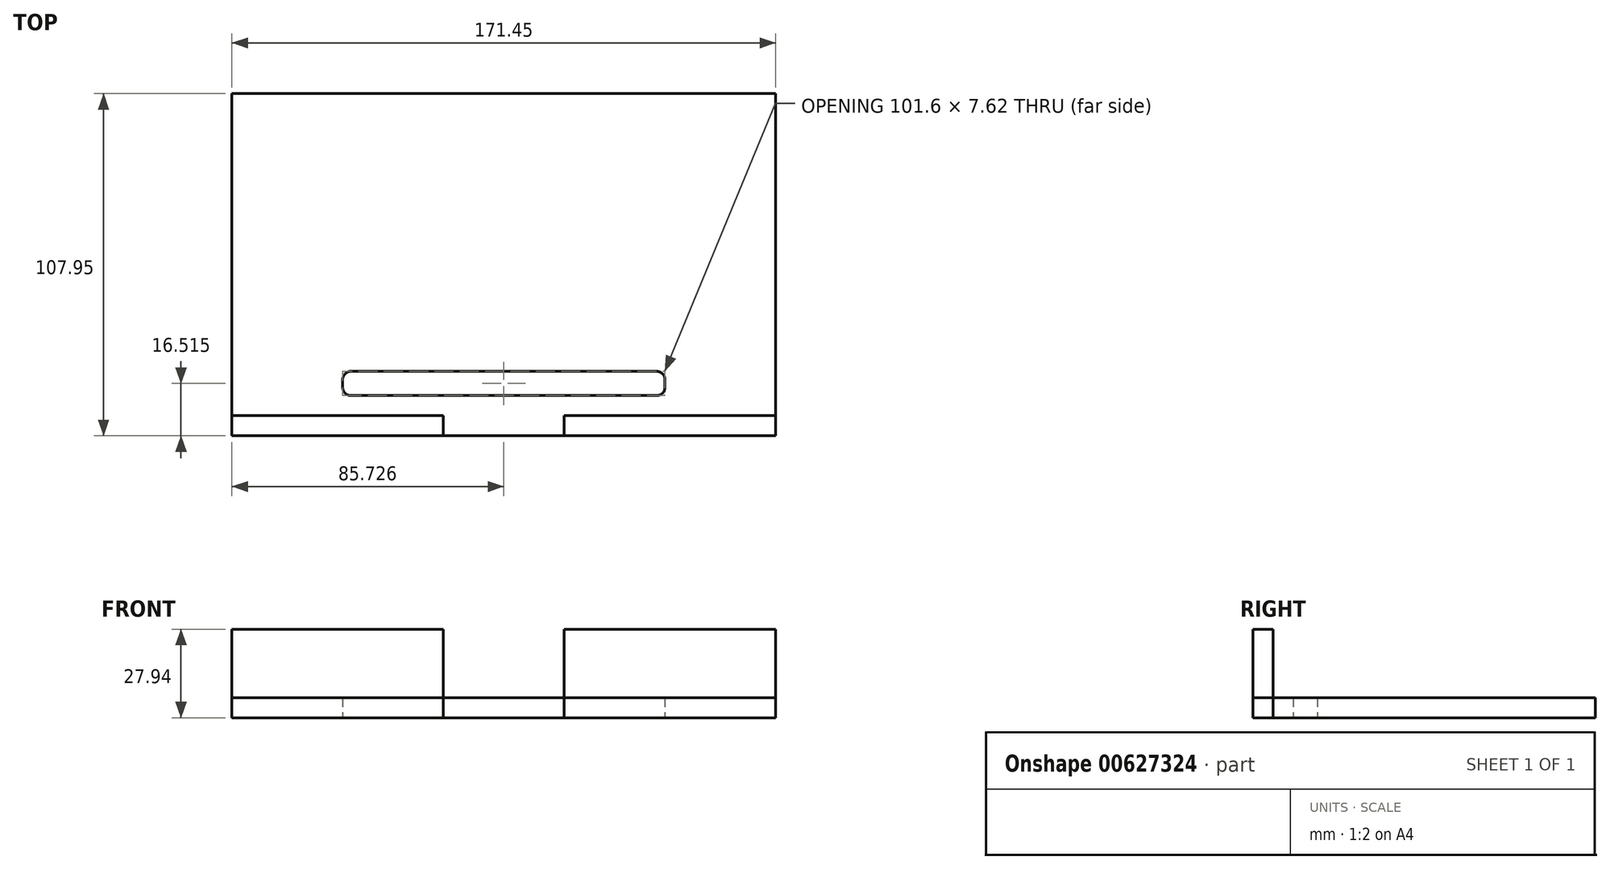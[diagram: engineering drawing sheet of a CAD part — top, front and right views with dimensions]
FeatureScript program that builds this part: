
annotation { "Feature Type Name" : "Feature", "Feature Type Description" : "" }
export const myFeature = defineFeature(function(context is Context, id is Id, definition is map)
    precondition{}
    {
        {
            var Q0;
            Q0=qCreatedBy(makeId("Top.planeOp"),FACE);
            var sketch = newSketch(context, id + "F0", { "sketchPlane" : qUnion([Q0])});
            skLineSegment(sketch, "E0.bottom", {"start": v(-115.82, 65.94) * mm, "end": v(55.63, 65.94) * mm});
            skLineSegment(sketch, "E0.top", {"start": v(-115.82, -42) * mm, "end": v(55.63, -42) * mm});
            skLineSegment(sketch, "E0.left", {"start": v(-115.82, 65.94) * mm, "end": v(-115.82, -42) * mm});
            skLineSegment(sketch, "E0.right", {"start": v(55.63, 65.94) * mm, "end": v(55.63, -42) * mm});
            skSolve(sketch);
        }
        {
            var Q0;
            Q0=qCreatedBy(makeId("Top.planeOp"),FACE);
            var sketch = newSketch(context, id + "F1", { "sketchPlane" : qUnion([Q0])});
            skLineSegment(sketch, "E1.bottom", {"start": v(-78.35, -29.3) * mm, "end": v(18.17, -29.3) * mm});
            skLineSegment(sketch, "E1.top", {"start": v(-78.35, -21.69) * mm, "end": v(18.17, -21.69) * mm});
            skLineSegment(sketch, "E1.left", {"start": v(-80.9, -26.77) * mm, "end": v(-80.9, -24.23) * mm});
            skLineSegment(sketch, "E1.right", {"start": v(20.7, -26.77) * mm, "end": v(20.7, -24.23) * mm});
            skPoint(sketch, "E2.visualSharp", {"position": v(-80.9, -21.69) * mm});
            skArc(sketch, "E2.filletArc", {"start": v(-78.35, -21.69) * mm, "mid": v(-80.15, -22.43) * mm, "end": v(-80.9, -24.23) * mm});
            skPoint(sketch, "E3.visualSharp", {"position": v(-80.9, -29.3) * mm});
            skArc(sketch, "E3.filletArc", {"start": v(-80.9, -26.77) * mm, "mid": v(-80.15, -28.56) * mm, "end": v(-78.35, -29.3) * mm});
            skPoint(sketch, "E4.visualSharp", {"position": v(20.7, -29.3) * mm});
            skArc(sketch, "E4.filletArc", {"start": v(18.17, -29.3) * mm, "mid": v(19.96, -28.56) * mm, "end": v(20.7, -26.77) * mm});
            skPoint(sketch, "E5.visualSharp", {"position": v(20.7, -21.69) * mm});
            skArc(sketch, "E5.filletArc", {"start": v(20.7, -24.23) * mm, "mid": v(19.96, -22.43) * mm, "end": v(18.17, -21.69) * mm});
            skSolve(sketch);
        }
        {
            var Q0;
            Q0=makeQuery(id+"F0.imprint","IMPRINT",FACE,{"disambiguationData":[TD([[makeQuery(id+"F0.imprint","IMPRINT",EDGE,{"derivedFrom":sQuery(id+"F0.wireOp",EDGE,"E0.bottom")}),-1.0]])]});
            var sketch = newSketch(context, id + "F2", { "sketchPlane" : qUnion([Q0])});
            skLineSegment(sketch, "E6.bottom", {"start": v(-115.82, -42) * mm, "end": v(-49.14, -42) * mm});
            skLineSegment(sketch, "E6.top", {"start": v(-115.82, -35.66) * mm, "end": v(-49.14, -35.66) * mm});
            skLineSegment(sketch, "E6.left", {"start": v(-115.82, -42) * mm, "end": v(-115.82, -35.66) * mm});
            skLineSegment(sketch, "E6.right", {"start": v(-49.14, -42) * mm, "end": v(-49.14, -35.66) * mm});
            skLineSegment(sketch, "E7.bottom", {"start": v(55.63, -42) * mm, "end": v(-11.04, -42) * mm});
            skLineSegment(sketch, "E7.top", {"start": v(55.63, -35.66) * mm, "end": v(-11.04, -35.66) * mm});
            skLineSegment(sketch, "E7.left", {"start": v(55.63, -42) * mm, "end": v(55.63, -35.66) * mm});
            skLineSegment(sketch, "E7.right", {"start": v(-11.04, -42) * mm, "end": v(-11.04, -35.66) * mm});
            skSolve(sketch);
        }
        {
            var Q0;
            Q0 = qSketchRegion(id + "F2", true);
            extrude(context, id + "F3", {"entities" : qUnion([Q0]), "depth" : 27.94 * mm, "offsetDistance" : 25.4 * mm});
        }
        {
            var Q0;
            Q0 = qSketchRegion(id + "F0", true);
            extrude(context, id + "F4", {"entities" : qUnion([Q0]), "depth" : 6.35 * mm, "offsetDistance" : 25.4 * mm});
        }
        {
            var Q0;
            Q0 = qSketchRegion(id + "F1", true);
            extrude(context, id + "F5", {"entities" : qUnion([Q0]), "operationType" : NewBodyOperationType.REMOVE, "depth" : 6.35 * mm, "offsetDistance" : 25.4 * mm});
        }
    });
